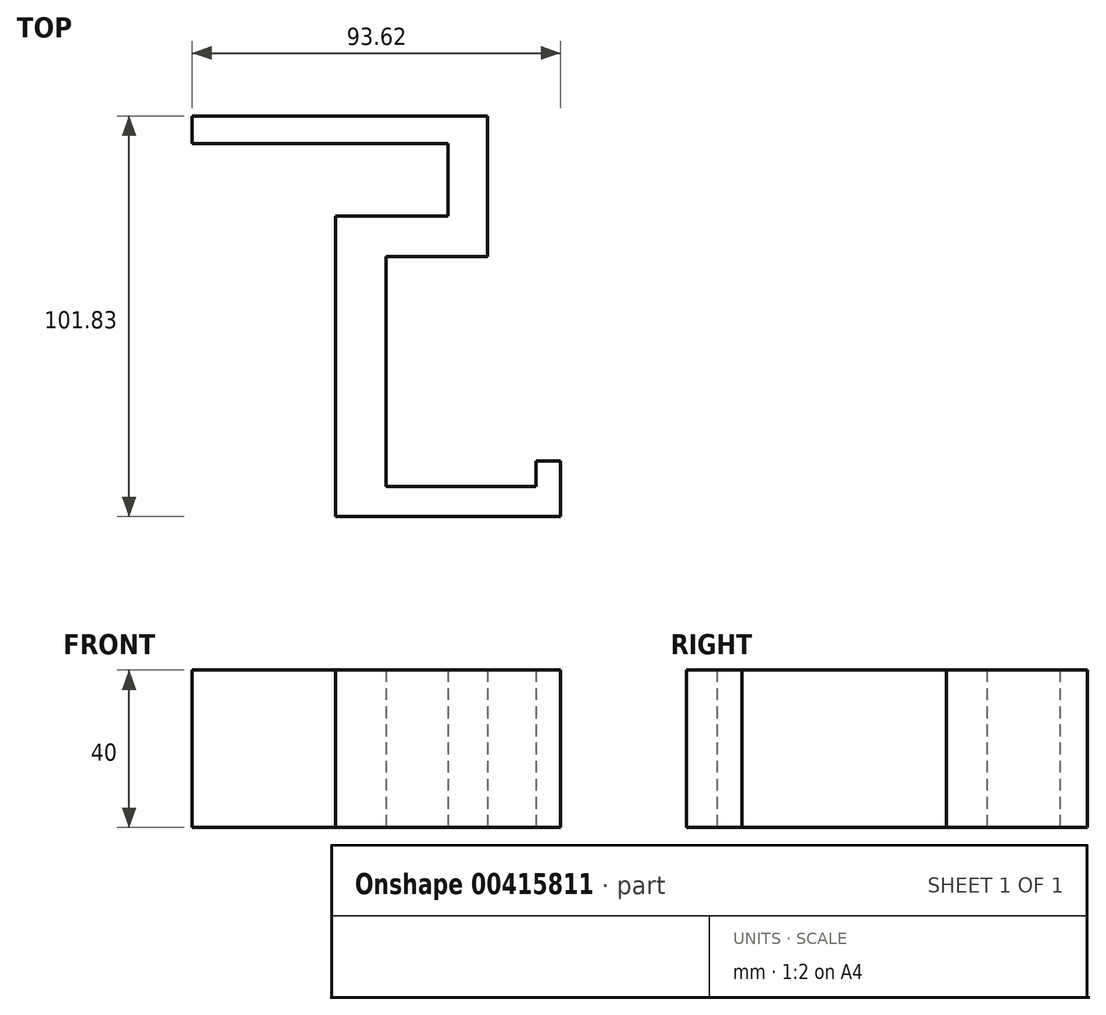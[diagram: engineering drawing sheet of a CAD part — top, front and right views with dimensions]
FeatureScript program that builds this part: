
annotation { "Feature Type Name" : "Feature", "Feature Type Description" : "" }
export const myFeature = defineFeature(function(context is Context, id is Id, definition is map)
    precondition{}
    {
        {
            var Q0;
            Q0=qCreatedBy(makeId("Top.planeOp"),FACE);
            var sketch = newSketch(context, id + "F0", { "sketchPlane" : qUnion([Q0])});
            skLineSegment(sketch, "E0", {"start": v(0, -18.5) * mm, "end": v(0, 0) * mm});
            skLineSegment(sketch, "E1", {"start": v(0, -18.5) * mm, "end": v(10, -18.5) * mm});
            skLineSegment(sketch, "E2", {"start": v(0, 0) * mm, "end": v(-65, 0) * mm});
            skLineSegment(sketch, "E3", {"start": v(-65, 0) * mm, "end": v(-65, 7) * mm});
            skLineSegment(sketch, "E4", {"start": v(10, -18.5) * mm, "end": v(10, 7) * mm});
            skLineSegment(sketch, "E5", {"start": v(10, 7) * mm, "end": v(-65, 7) * mm});
            skLineSegment(sketch, "E6", {"start": v(10, -12.74) * mm, "end": v(10, -18.5) * mm});
            skLineSegment(sketch, "E7", {"start": v(0, -18.5) * mm, "end": v(-28.58, -18.5) * mm});
            skLineSegment(sketch, "E8", {"start": v(-28.58, -18.5) * mm, "end": v(-28.58, -94.83) * mm});
            skLineSegment(sketch, "E9", {"start": v(-28.58, -94.83) * mm, "end": v(28.62, -94.83) * mm});
            skLineSegment(sketch, "E10", {"start": v(28.62, -94.83) * mm, "end": v(28.62, -87.11) * mm});
            skLineSegment(sketch, "E11", {"start": v(28.62, -87.11) * mm, "end": v(-15.77, -87.11) * mm});
            skLineSegment(sketch, "E12", {"start": v(-15.77, -87.11) * mm, "end": v(-15.77, -18.5) * mm});
            skLineSegment(sketch, "E13", {"start": v(10, -18.5) * mm, "end": v(10, -28.8) * mm});
            skLineSegment(sketch, "E14", {"start": v(10, -28.8) * mm, "end": v(-15.77, -28.8) * mm});
            skLineSegment(sketch, "E15", {"start": v(-15.77, -28.8) * mm, "end": v(-15.77, -87.11) * mm});
            skLineSegment(sketch, "E16", {"start": v(28.62, -87.11) * mm, "end": v(28.62, -80.73) * mm});
            skLineSegment(sketch, "E17", {"start": v(28.62, -80.73) * mm, "end": v(22.44, -80.73) * mm});
            skLineSegment(sketch, "E18", {"start": v(22.44, -80.73) * mm, "end": v(22.44, -87.11) * mm});
            skSolve(sketch);
        }
        {
            var Q0;
            Q0 = qSketchRegion(id + "F0", true);
            extrude(context, id + "F1", {"entities" : qUnion([Q0]), "depth" : 40 * mm, "offsetDistance" : 25.4 * mm});
        }
    });
